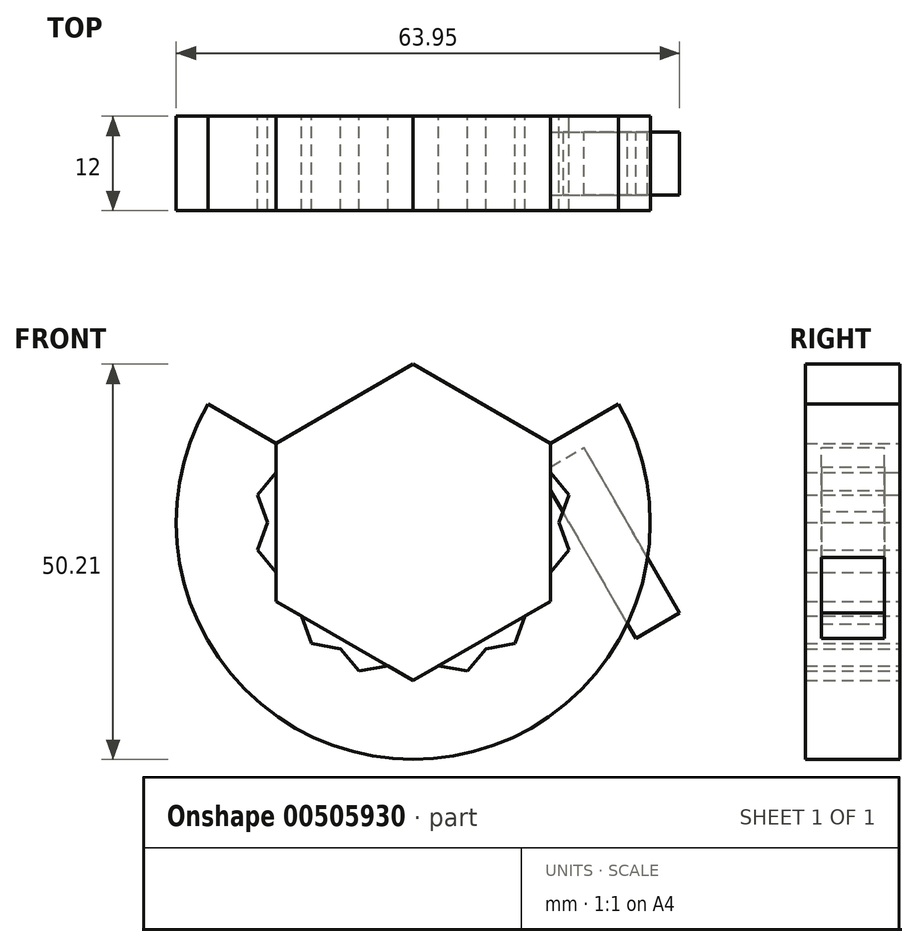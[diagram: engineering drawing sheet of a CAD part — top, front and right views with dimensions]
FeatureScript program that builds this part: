
annotation { "Feature Type Name" : "Feature", "Feature Type Description" : "" }
export const myFeature = defineFeature(function(context is Context, id is Id, definition is map)
    precondition{}
    {
        {
            var Q0;
            Q0=qCreatedBy(makeId("Front.planeOp"),FACE);
            var sketch = newSketch(context, id + "F0", { "sketchPlane" : qUnion([Q0])});
            skLineSegment(sketch, "E0.5", {"start": v(17.41, 8.3) * mm, "end": v(17.41, 4.58) * mm});
            skLineSegment(sketch, "E1.1.0", {"start": v(17.41, 4.58) * mm, "end": v(19.8, 1.74) * mm});
            skLineSegment(sketch, "E1.1.1", {"start": v(19.8, 1.74) * mm, "end": v(18.53, -1.75) * mm});
            skLineSegment(sketch, "E1.2.0", {"start": v(18.53, -1.75) * mm, "end": v(19.8, -5.25) * mm});
            skLineSegment(sketch, "E1.2.1", {"start": v(19.8, -5.25) * mm, "end": v(17.41, -8.1) * mm});
            skLineSegment(sketch, "E1.3.0", {"start": v(17.41, -8.1) * mm, "end": v(17.41, -11.8) * mm});
            skLineSegment(sketch, "E1.3.1", {"start": v(17.41, -11.8) * mm, "end": v(14.2, -13.67) * mm});
            skLineSegment(sketch, "E1.4.0", {"start": v(14.2, -13.67) * mm, "end": v(12.92, -17.16) * mm});
            skLineSegment(sketch, "E1.4.1", {"start": v(12.92, -17.16) * mm, "end": v(9.26, -17.8) * mm});
            skLineSegment(sketch, "E1.5.0", {"start": v(9.26, -17.8) * mm, "end": v(6.88, -20.65) * mm});
            skLineSegment(sketch, "E1.5.1", {"start": v(6.88, -20.65) * mm, "end": v(3.22, -20) * mm});
            skLineSegment(sketch, "E1.6.0", {"start": v(3.22, -20) * mm, "end": v(0, -21.86) * mm});
            skLineSegment(sketch, "E1.6.1", {"start": v(0, -21.86) * mm, "end": v(-3.22, -20) * mm});
            skLineSegment(sketch, "E1.7.0", {"start": v(-3.22, -20) * mm, "end": v(-6.88, -20.65) * mm});
            skLineSegment(sketch, "E1.7.1", {"start": v(-6.88, -20.65) * mm, "end": v(-9.26, -17.8) * mm});
            skLineSegment(sketch, "E1.8.0", {"start": v(-9.26, -17.8) * mm, "end": v(-12.92, -17.16) * mm});
            skLineSegment(sketch, "E1.8.1", {"start": v(-12.92, -17.16) * mm, "end": v(-14.2, -13.67) * mm});
            skLineSegment(sketch, "E1.9.0", {"start": v(-14.2, -13.67) * mm, "end": v(-17.41, -11.8) * mm});
            skLineSegment(sketch, "E2.1.0", {"start": v(-17.41, -11.8) * mm, "end": v(-17.41, -8.1) * mm});
            skLineSegment(sketch, "E2.1.1", {"start": v(-17.41, -8.1) * mm, "end": v(-19.8, -5.25) * mm});
            skLineSegment(sketch, "E2.2.0", {"start": v(-19.8, -5.25) * mm, "end": v(-18.53, -1.75) * mm});
            skLineSegment(sketch, "E2.2.1", {"start": v(-18.53, -1.75) * mm, "end": v(-19.8, 1.74) * mm});
            skLineSegment(sketch, "E2.3.0", {"start": v(-19.8, 1.74) * mm, "end": v(-17.41, 4.58) * mm});
            skLineSegment(sketch, "E2.3.1", {"start": v(-17.41, 4.58) * mm, "end": v(-17.41, 8.3) * mm});
            skPoint(sketch, "E2.center", {"position": v(0, -1.75) * mm});
            skArc(sketch, "E3", {"start": v(-26.07, 13.3) * mm, "mid": v(0, -31.86) * mm, "end": v(26.07, 13.3) * mm});
            skLineSegment(sketch, "E4", {"start": v(17.41, 8.3) * mm, "end": v(26.07, 13.3) * mm});
            skLineSegment(sketch, "E5.MirrorCS", {"start": v(-17.41, 8.3) * mm, "end": v(-26.07, 13.3) * mm});
            skPoint(sketch, "E6.orphan", {"position": v(-17.41, 8.3) * mm});
            skSolve(sketch);
        }
        {
            var Q0;
            Q0 = qSketchRegion(id + "F0", true);
            extrude(context, id + "F1", {"entities" : qUnion([Q0]), "depth" : 12 * mm});
        }
        {
            var Q0;
            Q0=makeQuery(id+"F1.opExtrude","CAP_FACE",FACE,{"disambiguationData":[OSD([sQuery(id+"F0.wireOp",EDGE,"E0.5"),sQuery(id+"F0.wireOp",EDGE,"E1.1.0"),sQuery(id+"F0.wireOp",EDGE,"E1.1.1"),sQuery(id+"F0.wireOp",EDGE,"E1.2.0"),sQuery(id+"F0.wireOp",EDGE,"E1.2.1"),sQuery(id+"F0.wireOp",EDGE,"E1.3.0"),sQuery(id+"F0.wireOp",EDGE,"E1.3.1"),sQuery(id+"F0.wireOp",EDGE,"E1.4.0"),sQuery(id+"F0.wireOp",EDGE,"E1.4.1"),sQuery(id+"F0.wireOp",EDGE,"E1.5.0"),sQuery(id+"F0.wireOp",EDGE,"E1.5.1"),sQuery(id+"F0.wireOp",EDGE,"E1.6.0"),sQuery(id+"F0.wireOp",EDGE,"E1.6.1"),sQuery(id+"F0.wireOp",EDGE,"E1.7.0"),sQuery(id+"F0.wireOp",EDGE,"E1.7.1"),sQuery(id+"F0.wireOp",EDGE,"E1.8.0"),sQuery(id+"F0.wireOp",EDGE,"E1.8.1"),sQuery(id+"F0.wireOp",EDGE,"E1.9.0"),sQuery(id+"F0.wireOp",EDGE,"E2.1.0"),sQuery(id+"F0.wireOp",EDGE,"E2.1.1"),sQuery(id+"F0.wireOp",EDGE,"E2.2.0"),sQuery(id+"F0.wireOp",EDGE,"E2.2.1"),sQuery(id+"F0.wireOp",EDGE,"E2.3.0"),sQuery(id+"F0.wireOp",EDGE,"E2.3.1"),sQuery(id+"F0.wireOp",EDGE,"E3"),sQuery(id+"F0.wireOp",EDGE,"E4"),sQuery(id+"F0.wireOp",EDGE,"E5.MirrorCS")])],"isStart":true});
            var sketch = newSketch(context, id + "F2", { "sketchPlane" : qUnion([Q0])});
            skArc(sketch, "E7.0", {"start": v(26.07, 13.3) * mm, "mid": v(0, -31.86) * mm, "end": v(-26.07, 13.3) * mm});
            skCircle(sketch, "E8.cCircle", {"center": v(0, -1.75) * mm, "radius": 17.41 * mm, "construction": true});
            skLineSegment(sketch, "E8.0", {"start": v(6.88, -20.65) * mm, "end": v(-12.92, -17.16) * mm});
            skLineSegment(sketch, "E8.1", {"start": v(-12.92, -17.16) * mm, "end": v(-19.8, 1.74) * mm});
            skLineSegment(sketch, "E8.2", {"start": v(-19.8, 1.74) * mm, "end": v(-6.88, 17.14) * mm});
            skLineSegment(sketch, "E8.3", {"start": v(-6.88, 17.14) * mm, "end": v(12.92, 13.65) * mm});
            skLineSegment(sketch, "E8.4", {"start": v(12.92, 13.65) * mm, "end": v(19.8, -5.25) * mm});
            skLineSegment(sketch, "E8.5", {"start": v(19.8, -5.25) * mm, "end": v(6.88, -20.65) * mm});
            skPoint(sketch, "E8.0.midPoint", {"position": v(0, -19.17) * mm});
            skSolve(sketch);
        }
        {
            var Q0;
            Q0 = qSketchRegion(id + "F2", true);
            extrude(context, id + "F3", {"entities" : qUnion([Q0]), "oppositeDirection" : true, "depth" : 12 * mm});
        }
        {
            var Q0;
            Q0=makeQuery(id+"F3.opExtrude","SWEPT_BODY",BODY,{"disambiguationData":[OSD([sQuery(id+"F2.wireOp",EDGE,"E8.0"),sQuery(id+"F2.wireOp",EDGE,"E8.1"),sQuery(id+"F2.wireOp",EDGE,"E8.2"),sQuery(id+"F2.wireOp",EDGE,"E8.3"),sQuery(id+"F2.wireOp",EDGE,"E8.4"),sQuery(id+"F2.wireOp",EDGE,"E8.5")])]});
            var Q1;
            Q1=makeQuery(id+"F1.opExtrude","SWEPT_FACE",FACE,{"disambiguationData":[OSD([sQuery(id+"F0.wireOp",EDGE,"E3")])]});
            transform(context, id + "F4", {"entities" : qUnion([Q0]), "transformType" : TransformType.ROTATION, "transformAxis" : qUnion([Q1]), "angle" : 160 * degree, "makeCopy" : false});
        }
        {
            var Q0;
            Q0=makeQuery(id+"F3.opExtrude","SWEPT_BODY",BODY,{"disambiguationData":[OSD([sQuery(id+"F2.wireOp",EDGE,"E8.0"),sQuery(id+"F2.wireOp",EDGE,"E8.1"),sQuery(id+"F2.wireOp",EDGE,"E8.2"),sQuery(id+"F2.wireOp",EDGE,"E8.3"),sQuery(id+"F2.wireOp",EDGE,"E8.4"),sQuery(id+"F2.wireOp",EDGE,"E8.5")])]});
            var Q1;
            Q1=makeQuery(id+"F1.opExtrude","SWEPT_FACE",FACE,{"disambiguationData":[OSD([sQuery(id+"F0.wireOp",EDGE,"E3")])]});
            transform(context, id + "F5", {"entities" : qUnion([Q0]), "transformType" : TransformType.ROTATION, "transformAxis" : qUnion([Q1]), "angle" : 20 * degree, "makeCopy" : true});
        }
        {
            var Q0;
            Q0=makeQuery(id+"F5.opPattern","COPY",BODY,{"derivedFrom":makeQuery(id+"F3.opExtrude","SWEPT_BODY",BODY,{"disambiguationData":[OSD([sQuery(id+"F2.wireOp",EDGE,"E8.0"),sQuery(id+"F2.wireOp",EDGE,"E8.1"),sQuery(id+"F2.wireOp",EDGE,"E8.2"),sQuery(id+"F2.wireOp",EDGE,"E8.3"),sQuery(id+"F2.wireOp",EDGE,"E8.4"),sQuery(id+"F2.wireOp",EDGE,"E8.5")])]}),"instanceName":"1"});
            var Q1;
            Q1=makeQuery(id+"F1.opExtrude","SWEPT_FACE",FACE,{"disambiguationData":[OSD([sQuery(id+"F0.wireOp",EDGE,"E3")])]});
            transform(context, id + "F6", {"entities" : qUnion([Q0]), "transformType" : TransformType.ROTATION, "transformAxis" : qUnion([Q1]), "angle" : 20 * degree, "makeCopy" : true});
        }
        {
            var Q0;
            Q0=makeQuery(id+"F1.opExtrude","CAP_FACE",FACE,{"disambiguationData":[OSD([sQuery(id+"F0.wireOp",EDGE,"E0.5"),sQuery(id+"F0.wireOp",EDGE,"E1.1.0"),sQuery(id+"F0.wireOp",EDGE,"E1.1.1"),sQuery(id+"F0.wireOp",EDGE,"E1.2.0"),sQuery(id+"F0.wireOp",EDGE,"E1.2.1"),sQuery(id+"F0.wireOp",EDGE,"E1.3.0"),sQuery(id+"F0.wireOp",EDGE,"E1.3.1"),sQuery(id+"F0.wireOp",EDGE,"E1.4.0"),sQuery(id+"F0.wireOp",EDGE,"E1.4.1"),sQuery(id+"F0.wireOp",EDGE,"E1.5.0"),sQuery(id+"F0.wireOp",EDGE,"E1.5.1"),sQuery(id+"F0.wireOp",EDGE,"E1.6.0"),sQuery(id+"F0.wireOp",EDGE,"E1.6.1"),sQuery(id+"F0.wireOp",EDGE,"E1.7.0"),sQuery(id+"F0.wireOp",EDGE,"E1.7.1"),sQuery(id+"F0.wireOp",EDGE,"E1.8.0"),sQuery(id+"F0.wireOp",EDGE,"E1.8.1"),sQuery(id+"F0.wireOp",EDGE,"E1.9.0"),sQuery(id+"F0.wireOp",EDGE,"E2.1.0"),sQuery(id+"F0.wireOp",EDGE,"E2.1.1"),sQuery(id+"F0.wireOp",EDGE,"E2.2.0"),sQuery(id+"F0.wireOp",EDGE,"E2.2.1"),sQuery(id+"F0.wireOp",EDGE,"E2.3.0"),sQuery(id+"F0.wireOp",EDGE,"E2.3.1"),sQuery(id+"F0.wireOp",EDGE,"E3"),sQuery(id+"F0.wireOp",EDGE,"E4"),sQuery(id+"F0.wireOp",EDGE,"E5.MirrorCS")])],"isStart":false});
            cPlane(context, id + "F7", {"entities" : qUnion([Q0]), "cplaneType" : CPlaneType.OFFSET, "offset" : 6 * mm, "oppositeDirection" : true, "width" : 150 * mm, "height" : 150 * mm});
        }
        {
            var Q0;
            Q0=qCreatedBy(id+"F7.planeOp",FACE);
            var sketch = newSketch(context, id + "F8", { "sketchPlane" : qUnion([Q0])});
            skLineSegment(sketch, "E9", {"start": v(17.41, 5.3) * mm, "end": v(17.41, 2.3) * mm});
            skPoint(sketch, "E10.0", {"position": v(17.41, 8.3) * mm});
            skLineSegment(sketch, "E11", {"start": v(17.41, 5.3) * mm, "end": v(21.69, 7.77) * mm});
            skLineSegment(sketch, "E12", {"start": v(21.69, 7.77) * mm, "end": v(23.36, 4.88) * mm});
            skLineSegment(sketch, "E13", {"start": v(17.41, 2.3) * mm, "end": v(28.26, -16.5) * mm});
            skLineSegment(sketch, "E14", {"start": v(28.26, -16.5) * mm, "end": v(33.84, -13.28) * mm});
            skLineSegment(sketch, "E15", {"start": v(33.84, -13.28) * mm, "end": v(23.36, 4.88) * mm});
            skArc(sketch, "E16.0", {"start": v(-26.07, 13.3) * mm, "mid": v(0, -31.86) * mm, "end": v(26.07, 13.3) * mm});
            skCircle(sketch, "E17", {"center": v(0, -1.75) * mm, "radius": 20.1 * mm, "construction": true});
            skSolve(sketch);
        }
        {
            var Q0;
            Q0 = qSketchRegion(id + "F8", true);
            extrude(context, id + "F9", {"entities" : qUnion([Q0]), "depth" : 8 * mm, "symmetric" : true});
        }
        {
            var Q0;
            Q0=makeQuery(id+"F9.opExtrude","SWEPT_BODY",BODY,{"disambiguationData":[OSD([sQuery(id+"F8.wireOp",EDGE,"E9"),sQuery(id+"F8.wireOp",EDGE,"E11"),sQuery(id+"F8.wireOp",EDGE,"E12"),sQuery(id+"F8.wireOp",EDGE,"E13"),sQuery(id+"F8.wireOp",EDGE,"E14"),sQuery(id+"F8.wireOp",EDGE,"E15")])]});
            var Q1;
            Q1=makeQuery(id+"F1.opExtrude","SWEPT_BODY",BODY,{"disambiguationData":[OSD([sQuery(id+"F0.wireOp",EDGE,"E0.5"),sQuery(id+"F0.wireOp",EDGE,"E1.1.0"),sQuery(id+"F0.wireOp",EDGE,"E1.1.1"),sQuery(id+"F0.wireOp",EDGE,"E1.2.0"),sQuery(id+"F0.wireOp",EDGE,"E1.2.1"),sQuery(id+"F0.wireOp",EDGE,"E1.3.0"),sQuery(id+"F0.wireOp",EDGE,"E1.3.1"),sQuery(id+"F0.wireOp",EDGE,"E1.4.0"),sQuery(id+"F0.wireOp",EDGE,"E1.4.1"),sQuery(id+"F0.wireOp",EDGE,"E1.5.0"),sQuery(id+"F0.wireOp",EDGE,"E1.5.1"),sQuery(id+"F0.wireOp",EDGE,"E1.6.0"),sQuery(id+"F0.wireOp",EDGE,"E1.6.1"),sQuery(id+"F0.wireOp",EDGE,"E1.7.0"),sQuery(id+"F0.wireOp",EDGE,"E1.7.1"),sQuery(id+"F0.wireOp",EDGE,"E1.8.0"),sQuery(id+"F0.wireOp",EDGE,"E1.8.1"),sQuery(id+"F0.wireOp",EDGE,"E1.9.0"),sQuery(id+"F0.wireOp",EDGE,"E2.1.0"),sQuery(id+"F0.wireOp",EDGE,"E2.1.1"),sQuery(id+"F0.wireOp",EDGE,"E2.2.0"),sQuery(id+"F0.wireOp",EDGE,"E2.2.1"),sQuery(id+"F0.wireOp",EDGE,"E2.3.0"),sQuery(id+"F0.wireOp",EDGE,"E2.3.1"),sQuery(id+"F0.wireOp",EDGE,"E3"),sQuery(id+"F0.wireOp",EDGE,"E4"),sQuery(id+"F0.wireOp",EDGE,"E5.MirrorCS")])]});
            booleanBodies(context, id + "F10", {"operationType" : BooleanOperationType.SUBTRACTION, "tools" : qUnion([Q0]), "targets" : qUnion([Q1]), "keepTools" : true});
        }
        {
            var Q0;
            Q0=makeQuery(id+"F5.opPattern","COPY",BODY,{"derivedFrom":makeQuery(id+"F3.opExtrude","SWEPT_BODY",BODY,{"disambiguationData":[OSD([sQuery(id+"F2.wireOp",EDGE,"E8.0"),sQuery(id+"F2.wireOp",EDGE,"E8.1"),sQuery(id+"F2.wireOp",EDGE,"E8.2"),sQuery(id+"F2.wireOp",EDGE,"E8.3"),sQuery(id+"F2.wireOp",EDGE,"E8.4"),sQuery(id+"F2.wireOp",EDGE,"E8.5")])]}),"instanceName":"1"});
            var Q1;
            Q1=makeQuery(id+"F6.opPattern","COPY",BODY,{"derivedFrom":makeQuery(id+"F5.opPattern","COPY",BODY,{"derivedFrom":makeQuery(id+"F3.opExtrude","SWEPT_BODY",BODY,{"disambiguationData":[OSD([sQuery(id+"F2.wireOp",EDGE,"E8.0"),sQuery(id+"F2.wireOp",EDGE,"E8.1"),sQuery(id+"F2.wireOp",EDGE,"E8.2"),sQuery(id+"F2.wireOp",EDGE,"E8.3"),sQuery(id+"F2.wireOp",EDGE,"E8.4"),sQuery(id+"F2.wireOp",EDGE,"E8.5")])]}),"instanceName":"1"}),"instanceName":"1"});
            deleteBodies(context, id + "F11", {"entities" : qUnion([Q0, Q1])});
        }
    });
